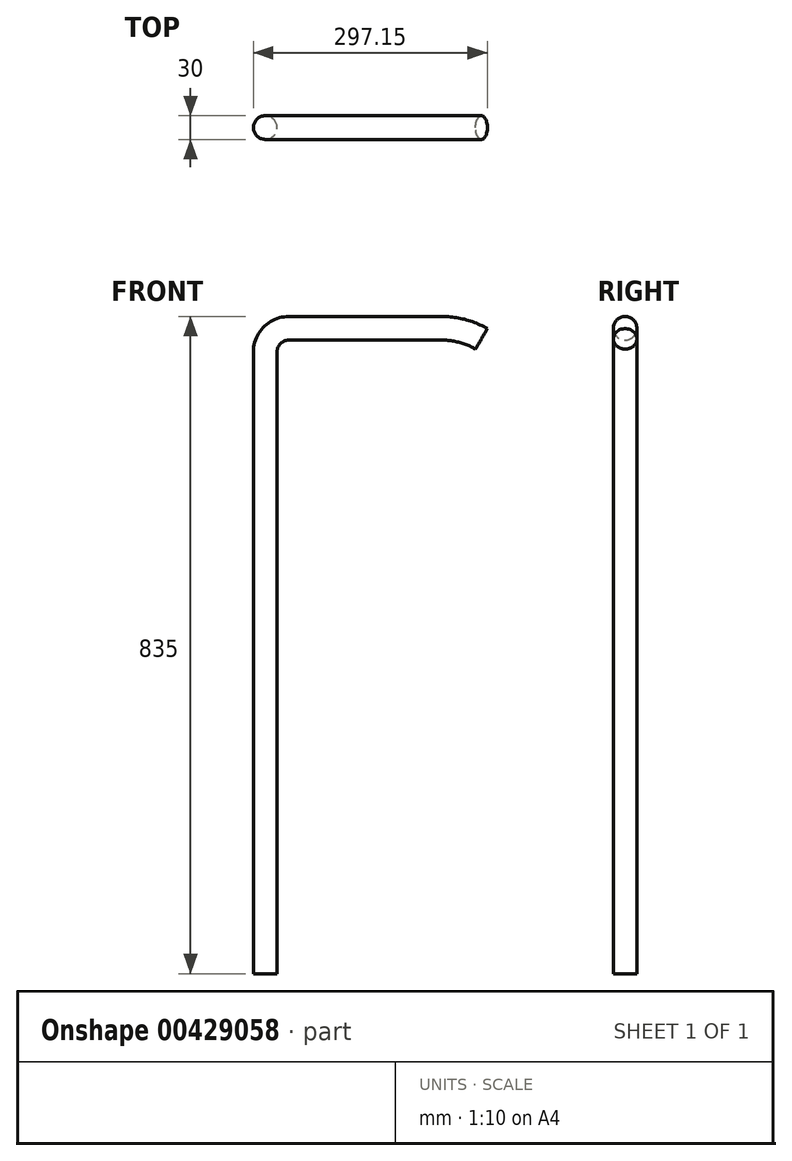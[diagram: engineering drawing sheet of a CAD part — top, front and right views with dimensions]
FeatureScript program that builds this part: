
annotation { "Feature Type Name" : "Feature", "Feature Type Description" : "" }
export const myFeature = defineFeature(function(context is Context, id is Id, definition is map)
    precondition{}
    {
        {
            var Q0;
            Q0=qCreatedBy(makeId("Front.planeOp"),FACE);
            var sketch = newSketch(context, id + "F0", { "sketchPlane" : qUnion([Q0])});
            skLineSegment(sketch, "E0", {"start": v(0, 0) * mm, "end": v(0, 790) * mm});
            skLineSegment(sketch, "E1", {"start": v(30, 820) * mm, "end": v(224.65, 820) * mm});
            skPoint(sketch, "E2.visualSharp", {"position": v(0, 820) * mm});
            skArc(sketch, "E2.filletArc", {"start": v(30, 820) * mm, "mid": v(8.79, 811.21) * mm, "end": v(0, 790) * mm});
            skLineSegment(sketch, "E3", {"start": v(274.65, 806.6) * mm, "end": v(277, 805.25) * mm});
            skPoint(sketch, "E4.orphan", {"position": v(277, 820) * mm});
            skPoint(sketch, "E5.visualSharp", {"position": v(251.45, 820) * mm});
            skArc(sketch, "E5.filletArc", {"start": v(274.65, 806.6) * mm, "mid": v(250.53, 816.6) * mm, "end": v(224.65, 820) * mm});
            skSolve(sketch);
        }
        {
            var Q0;
            Q0=qCreatedBy(makeId("Top.planeOp"),FACE);
            var sketch = newSketch(context, id + "F1", { "sketchPlane" : qUnion([Q0])});
            skCircle(sketch, "E6", {"center": v(0, 0) * mm, "radius": 15 * mm});
            skSolve(sketch);
        }
        {
            var Q0;
            Q0=makeQuery(id+"F1.imprint","IMPRINT",FACE,{"disambiguationData":[TD([[makeQuery(id+"F1.imprint","IMPRINT",EDGE,{"derivedFrom":sQuery(id+"F1.wireOp",EDGE,"E6")}),1.0]])]});
            var Q1;
            Q1=sQuery(id+"F0.wireOp",EDGE,"E0");
            var Q2;
            Q2=sQuery(id+"F0.wireOp",EDGE,"E2.filletArc");
            var Q3;
            Q3=sQuery(id+"F0.wireOp",EDGE,"E1");
            var Q4;
            Q4=sQuery(id+"F0.wireOp",EDGE,"E5.filletArc");
            sweep(context, id + "F2", {"profiles" : qUnion([Q0]), "path" : qUnion([Q1, Q2, Q3, Q4])});
        }
    });
